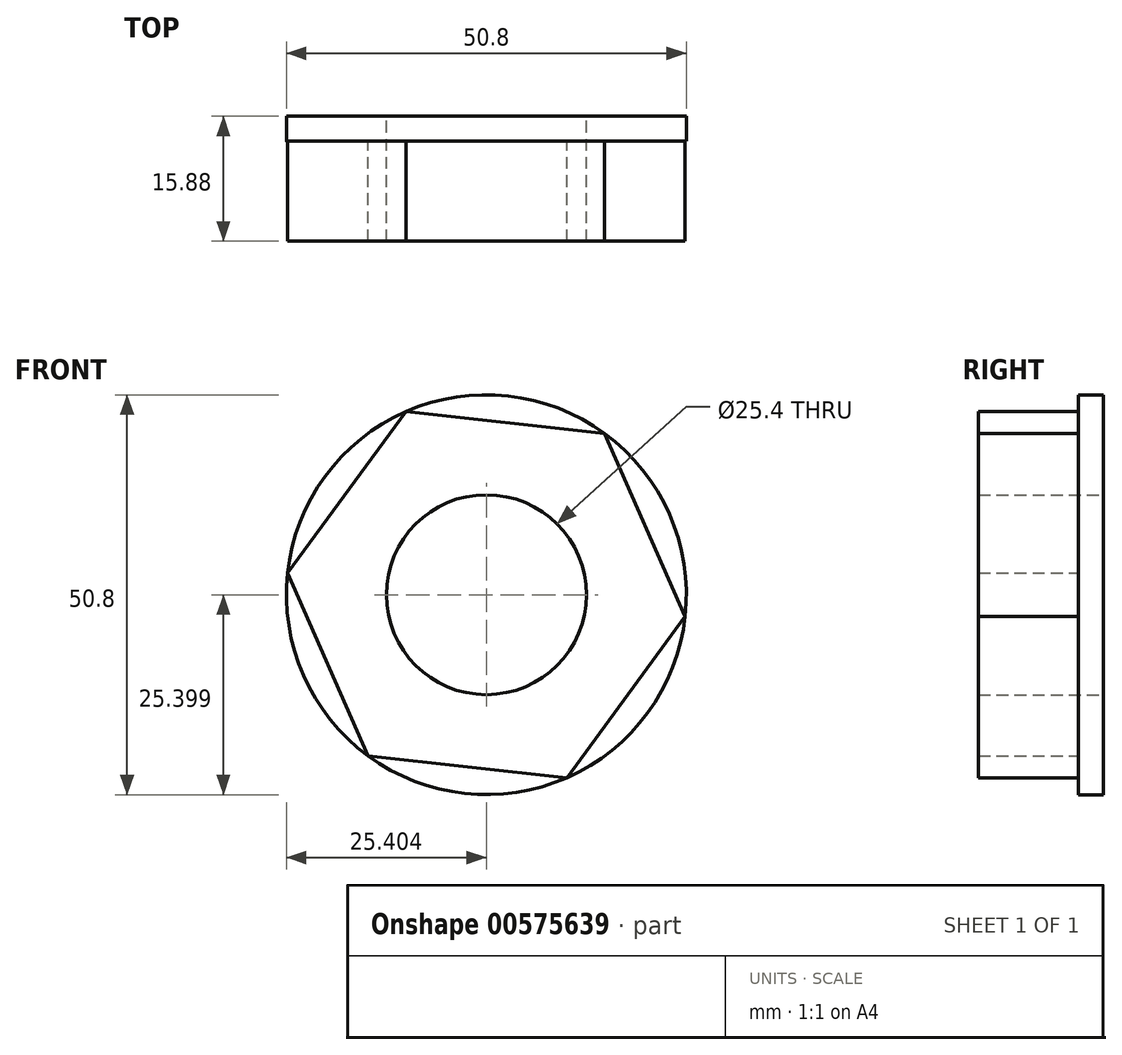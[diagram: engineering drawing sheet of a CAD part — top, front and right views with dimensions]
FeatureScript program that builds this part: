
annotation { "Feature Type Name" : "Feature", "Feature Type Description" : "" }
export const myFeature = defineFeature(function(context is Context, id is Id, definition is map)
    precondition{}
    {
        {
            var Q0;
            Q0=qCreatedBy(makeId("Front.planeOp"),FACE);
            var sketch = newSketch(context, id + "F0", { "sketchPlane" : qUnion([Q0])});
            skCircle(sketch, "E0", {"center": v(-49.28, 2.03) * mm, "radius": 12.7 * mm});
            skCircle(sketch, "E1.0", {"center": v(-49.28, 2.03) * mm, "radius": 25.4 * mm});
            skSolve(sketch);
        }
        {
            var Q0;
            Q0=qSketchRegion(id+"F0",true);
            extrude(context, id + "F1", {"entities" : qUnion([Q0]), "depth" : 3.17 * mm, "offsetDistance" : 25.4 * mm});
        }
        {
            var Q0;
            Q0=makeQuery(id+"F1.opExtrude","CAP_FACE",FACE,{"disambiguationData":[OSD([sQuery(id+"F0.wireOp",EDGE,"E0"),sQuery(id+"F0.wireOp",EDGE,"E1.0")])],"isStart":false});
            var sketch = newSketch(context, id + "F2", { "sketchPlane" : qUnion([Q0])});
            skCircle(sketch, "E2", {"center": v(-49.28, 2.03) * mm, "radius": 12.7 * mm});
            skCircle(sketch, "E3.cCircle", {"center": v(-49.28, 2.03) * mm, "radius": 25.4 * mm, "construction": true});
            skLineSegment(sketch, "E3.0", {"start": v(-24.03, -0.73) * mm, "end": v(-39.04, -21.22) * mm});
            skLineSegment(sketch, "E3.1", {"start": v(-39.04, -21.22) * mm, "end": v(-64.29, -18.46) * mm});
            skLineSegment(sketch, "E3.2", {"start": v(-64.29, -18.46) * mm, "end": v(-74.53, 4.79) * mm});
            skLineSegment(sketch, "E3.3", {"start": v(-74.53, 4.79) * mm, "end": v(-59.51, 25.27) * mm});
            skLineSegment(sketch, "E3.4", {"start": v(-59.51, 25.27) * mm, "end": v(-34.26, 22.52) * mm});
            skLineSegment(sketch, "E3.5", {"start": v(-34.26, 22.52) * mm, "end": v(-24.03, -0.73) * mm});
            skSolve(sketch);
        }
        {
            var Q0;
            Q0=qSketchRegion(id+"F2",true);
            extrude(context, id + "F3", {"entities" : qUnion([Q0]), "operationType" : NewBodyOperationType.ADD, "depth" : 12.7 * mm, "offsetDistance" : 25.4 * mm});
        }
    });
